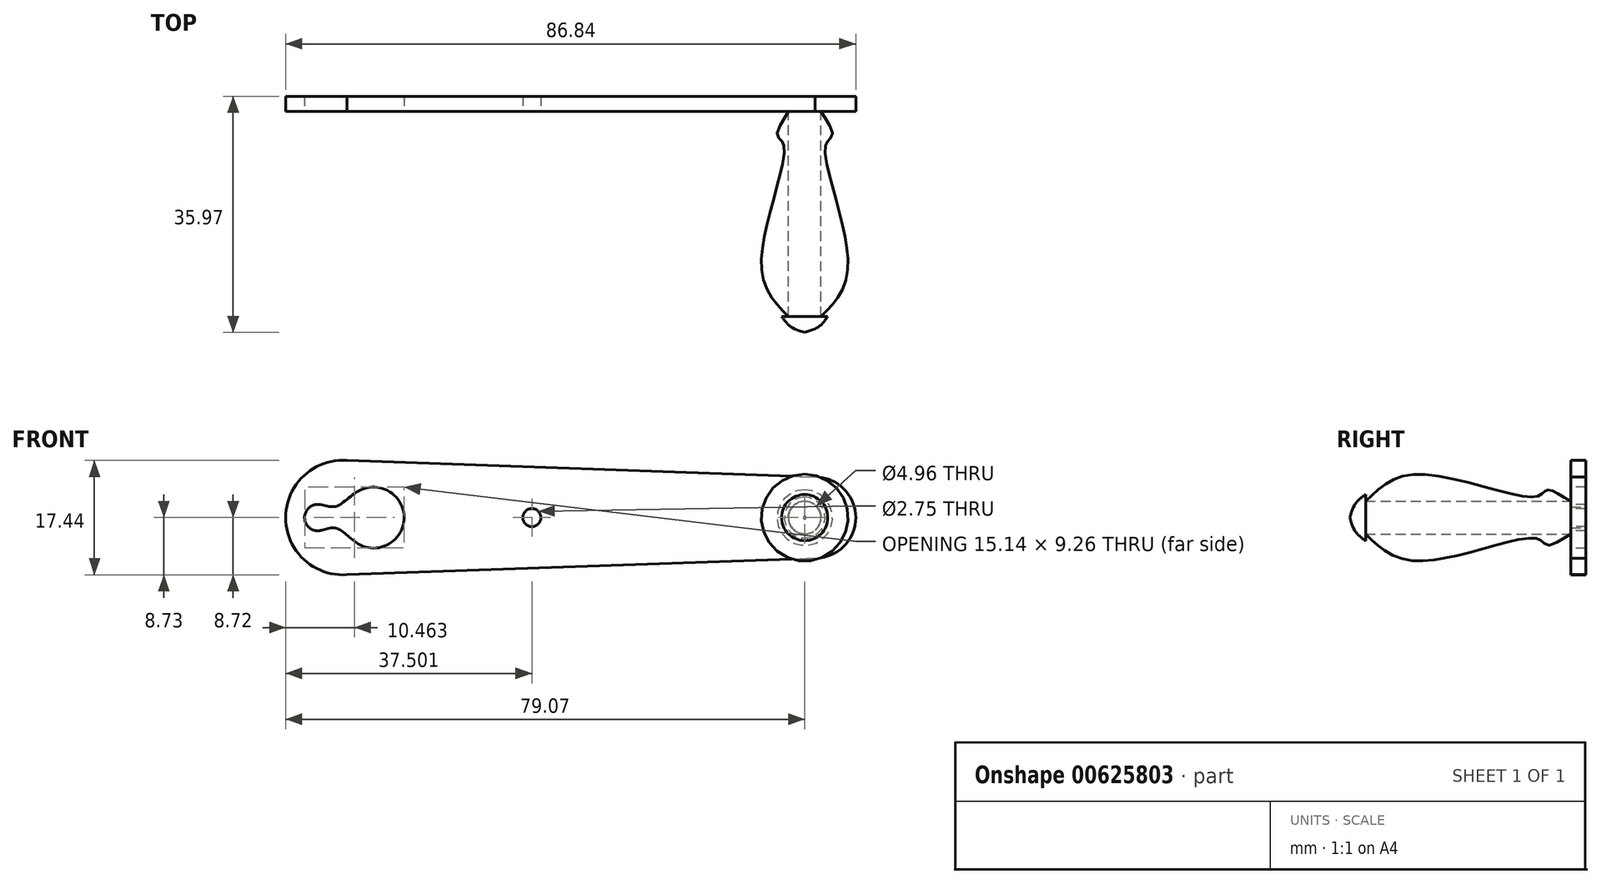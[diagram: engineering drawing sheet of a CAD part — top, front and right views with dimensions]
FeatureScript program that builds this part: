
annotation { "Feature Type Name" : "Feature", "Feature Type Description" : "" }
export const myFeature = defineFeature(function(context is Context, id is Id, definition is map)
    precondition{}
    {
        {
            var Q0;
            Q0=qCreatedBy(makeId("Front.planeOp"),FACE);
            var sketch = newSketch(context, id + "F0", { "sketchPlane" : qUnion([Q0])});
            skArc(sketch, "E0", {"start": v(-40.37, 8.7) * mm, "mid": v(-49.7, 0) * mm, "end": v(-40.37, -8.7) * mm});
            skArc(sketch, "E1", {"start": v(30.95, -6.18) * mm, "mid": v(37.13, 0) * mm, "end": v(30.95, 6.18) * mm});
            skLineSegment(sketch, "E2", {"start": v(-40.99, 8.72) * mm, "end": v(30.95, 6.18) * mm});
            skLineSegment(sketch, "E3", {"start": v(-40.99, -8.72) * mm, "end": v(30.95, -6.18) * mm});
            skSolve(sketch);
        }
        {
            var Q0;
            Q0 = qSketchRegion(id + "F0", true);
            extrude(context, id + "F1", {"entities" : qUnion([Q0]), "depth" : 2.3 * mm, "offsetDistance" : 25 * mm});
        }
        {
            var Q0;
            Q0=makeQuery(id+"F1.opExtrude","CAP_FACE",FACE,{"disambiguationData":[OSD([sQuery(id+"F0.wireOp",EDGE,"E0"),sQuery(id+"F0.wireOp",EDGE,"E1"),sQuery(id+"F0.wireOp",EDGE,"E2"),sQuery(id+"F0.wireOp",EDGE,"E3")])],"isStart":false});
            var sketch = newSketch(context, id + "F2", { "sketchPlane" : qUnion([Q0])});
            skCircle(sketch, "E4", {"center": v(-44.83, 0) * mm, "radius": 2 * mm});
            skCircle(sketch, "E5", {"center": v(-36.31, 0) * mm, "radius": 4.64 * mm});
            skPoint(sketch, "E6", {"position": v(-46.83, 0) * mm});
            skPoint(sketch, "E7", {"position": v(-31.67, 0) * mm});
            skPoint(sketch, "E8", {"position": v(-12.2, 0) * mm});
            skCircle(sketch, "E9", {"center": v(-12.2, 0) * mm, "radius": 1.38 * mm});
            skCircle(sketch, "E10", {"center": v(29.35, 0) * mm, "radius": 2.5 * mm});
            skFitSpline(sketch, "E11", {"points": [v(-44.74, 2) * mm, v(-42.08, 1.7) * mm, v(-38.53, 4.08) * mm], "startDerivative": vector(7.35, -0.33) * mm, "endDerivative": vector(8.19, 4.45) * mm});
            skFitSpline(sketch, "E12", {"points": [v(-44.28, -1.92) * mm, v(-41.92, -1.64) * mm, v(-39.06, -3.75) * mm], "startDerivative": vector(5.48, 1.58) * mm, "endDerivative": vector(6.13, -4.49) * mm});
            skSolve(sketch);
        }
        {
            var Q0;
            {var subQ0=sQuery(id+"F2.wireOp",EDGE,"E5");var subQ1=makeQuery(id+"F2.imprint","INTERSECT",VERTEX,{"derivedFrom":[subQ0,sQuery(id+"F2.wireOp",EDGE,"JXqlM0UY-bxi7-qLzu-tcPN-rijKCx4FC96E")]});Q0=makeQuery(id+"F2.imprint","IMPRINT",FACE,{"disambiguationData":[TD([[makeQuery(id+"F2.imprint","IMPRINT",EDGE,{"disambiguationData":[TD([[subQ1,-1.0]])],"derivedFrom":subQ0}),1.0]])]});}
            var Q1;
            {var subQ0=sQuery(id+"F2.wireOp",EDGE,"E4");var subQ1=makeQuery(id+"F2.imprint","INTERSECT",VERTEX,{"derivedFrom":[subQ0,sQuery(id+"F2.wireOp",EDGE,"JXqlM0UY-bxi7-qLzu-tcPN-rijKCx4FC96E")]});Q1=makeQuery(id+"F2.imprint","IMPRINT",FACE,{"disambiguationData":[TD([[makeQuery(id+"F2.imprint","IMPRINT",EDGE,{"disambiguationData":[TD([[subQ1,-1.0]])],"derivedFrom":subQ0}),1.0]])]});}
            var Q2;
            {var subQ0=sQuery(id+"F2.wireOp",EDGE,"JXqlM0UY-bxi7-qLzu-tcPN-rijKCx4FC96E");Q2=makeQuery(id+"F2.imprint","IMPRINT",FACE,{"disambiguationData":[TD([[makeQuery(id+"F2.imprint","IMPRINT",EDGE,{"derivedFrom":subQ0}),-1.0]])]});}
            var Q3;
            Q3=makeQuery(id+"F2.imprint","IMPRINT",FACE,{"disambiguationData":[TD([[makeQuery(id+"F2.imprint","IMPRINT",EDGE,{"derivedFrom":sQuery(id+"F2.wireOp",EDGE,"E9")}),1.0]])]});
            var Q4;
            {var subQ0=sQuery(id+"F2.wireOp",EDGE,"E11");Q4=makeQuery(id+"F2.imprint","IMPRINT",FACE,{"disambiguationData":[TD([[makeQuery(id+"F2.imprint","IMPRINT",EDGE,{"derivedFrom":subQ0}),-1.0]])]});}
            extrude(context, id + "F3", {"entities" : qUnion([Q0, Q1, Q2, Q3, Q4]), "operationType" : NewBodyOperationType.REMOVE, "endBound" : BoundingType.UP_TO_NEXT, "oppositeDirection" : true, "depth" : 25 * mm, "offsetDistance" : 25 * mm});
        }
        {
            var Q0;
            Q0=makeQuery(id+"F2.imprint","IMPRINT",FACE,{"disambiguationData":[TD([[makeQuery(id+"F2.imprint","IMPRINT",EDGE,{"derivedFrom":sQuery(id+"F2.wireOp",EDGE,"E10")}),1.0]])]});
            extrude(context, id + "F4", {"entities" : qUnion([Q0]), "operationType" : NewBodyOperationType.ADD, "depth" : 31.27 * mm, "offsetDistance" : 25 * mm});
        }
        {
            var Q0;
            Q0=qCreatedBy(makeId("Top.planeOp"),FACE);
            var sketch = newSketch(context, id + "F5", { "sketchPlane" : qUnion([Q0])});
            skFitSpline(sketch, "E13", {"points": [v(31.84, -2.3) * mm, v(33.57, -5.94) * mm, v(32.54, -7.52) * mm, v(35.97, -25.41) * mm, v(31.84, -33.56) * mm], "startDerivative": vector(14.04, -23.1) * mm, "endDerivative": vector(-21.7, -21.75) * mm});
            skLineSegment(sketch, "E14.0", {"start": v(30.95, -2.3) * mm, "end": v(37.13, -2.3) * mm});
            skLineSegment(sketch, "E15", {"start": v(31.84, -2.3) * mm, "end": v(31.84, -33.56) * mm});
            skLineSegment(sketch, "E16", {"start": v(29.36, -2.32) * mm, "end": v(29.36, -33.41) * mm, "construction": true});
            skLineSegment(sketch, "E17", {"start": v(29.36, -35.97) * mm, "end": v(29.36, -33.41) * mm});
            skFitSpline(sketch, "E18", {"points": [v(29.36, -35.97) * mm, v(31.47, -35.12) * mm, v(32.88, -33.56) * mm], "startDerivative": vector(4.46, 1.28) * mm, "endDerivative": vector(2.56, 3.56) * mm});
            skLineSegment(sketch, "E19", {"start": v(31.84, -33.56) * mm, "end": v(32.88, -33.56) * mm});
            skLineSegment(sketch, "E20", {"start": v(29.36, -33.57) * mm, "end": v(32.88, -33.56) * mm});
            skSolve(sketch);
        }
        {
            var Q0;
            Q0=makeQuery(id+"F5.imprint","IMPRINT",FACE,{"disambiguationData":[TD([[makeQuery(id+"F5.imprint","IMPRINT",EDGE,{"derivedFrom":sQuery(id+"F5.wireOp",EDGE,"E13")}),-1.0]])]});
            var Q1;
            Q1=sQuery(id+"F5.wireOp",EDGE,"E13");
            var Q2;
            Q2=sQuery(id+"F5.wireOp",EDGE,"E16");
            revolve(context, id + "F6", {"entities" : qUnion([Q0]), "surfaceEntities" : qUnion([Q1]), "axis" : qUnion([Q2]), "revolveType" : RevolveType.FULL});
        }
        {
            var Q0;
            {var subQ0=sQuery(id+"F5.wireOp",EDGE,"E18");Q0=makeQuery(id+"F5.imprint","IMPRINT",FACE,{"disambiguationData":[TD([[makeQuery(id+"F5.imprint","IMPRINT",EDGE,{"derivedFrom":subQ0}),1.0]])]});}
            var Q1;
            Q1=sQuery(id+"F5.wireOp",EDGE,"E16");
            revolve(context, id + "F7", {"operationType" : NewBodyOperationType.ADD, "entities" : qUnion([Q0]), "axis" : qUnion([Q1]), "revolveType" : RevolveType.FULL});
        }
    });
